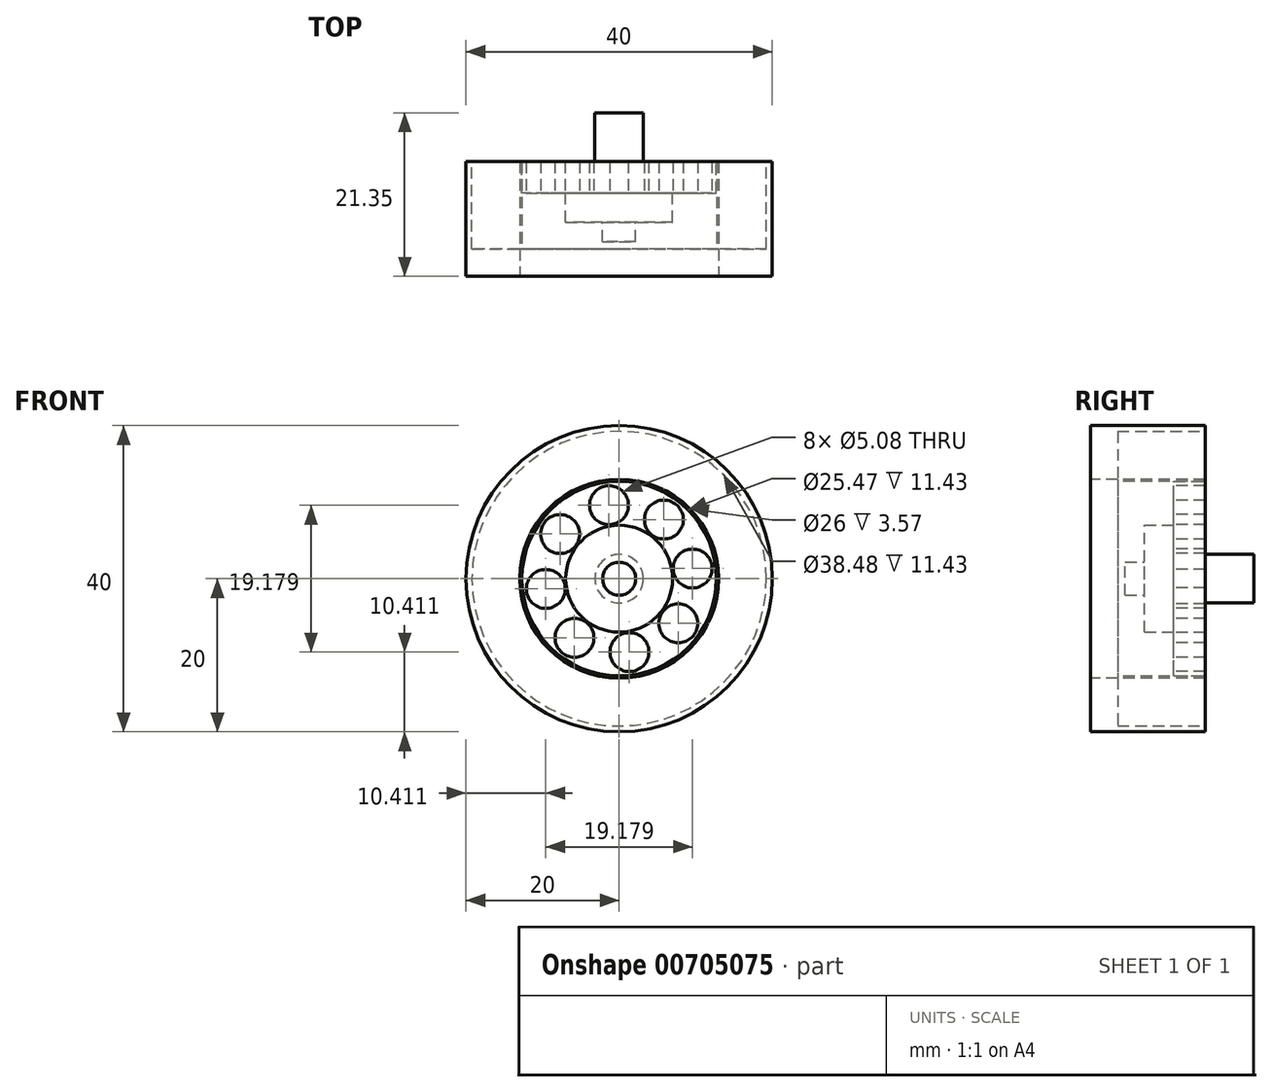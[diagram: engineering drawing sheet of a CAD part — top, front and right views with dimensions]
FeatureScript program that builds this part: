
annotation { "Feature Type Name" : "Feature", "Feature Type Description" : "" }
export const myFeature = defineFeature(function(context is Context, id is Id, definition is map)
    precondition{}
    {
        {
            var Q0;
            Q0=qCreatedBy(makeId("Front.planeOp"),FACE);
            var sketch = newSketch(context, id + "F0", { "sketchPlane" : qUnion([Q0])});
            skCircle(sketch, "E0", {"center": v(0, 0) * mm, "radius": 20 * mm});
            skCircle(sketch, "E1", {"center": v(-7.72, 5.84) * mm, "radius": 2.54 * mm});
            skCircle(sketch, "E2.1.0", {"center": v(-9.59, -1.33) * mm, "radius": 2.54 * mm});
            skCircle(sketch, "E2.2.0", {"center": v(-5.84, -7.72) * mm, "radius": 2.54 * mm});
            skCircle(sketch, "E2.3.0", {"center": v(1.33, -9.59) * mm, "radius": 2.54 * mm});
            skCircle(sketch, "E2.4.0", {"center": v(7.72, -5.84) * mm, "radius": 2.54 * mm});
            skCircle(sketch, "E2.5.0", {"center": v(9.59, 1.33) * mm, "radius": 2.54 * mm});
            skCircle(sketch, "E2.6.0", {"center": v(5.84, 7.72) * mm, "radius": 2.54 * mm});
            skCircle(sketch, "E2.7.0", {"center": v(-1.33, 9.59) * mm, "radius": 2.54 * mm});
            skSolve(sketch);
        }
        {
            var Q0;
            Q0=makeQuery(id+"F0.imprint","IMPRINT",FACE,{"disambiguationData":[TD([[makeQuery(id+"F0.imprint","IMPRINT",EDGE,{"derivedFrom":sQuery(id+"F0.wireOp",EDGE,"E0")}),1.0]])]});
            extrude(context, id + "F1", {"entities" : qUnion([Q0]), "oppositeDirection" : true, "depth" : 15 * mm, "offsetDistance" : 25.4 * mm});
        }
        {
            var Q0;
            Q0=makeQuery(id+"F0.imprint","IMPRINT",FACE,{"disambiguationData":[TD([[makeQuery(id+"F0.imprint","IMPRINT",EDGE,{"derivedFrom":sQuery(id+"F0.wireOp",EDGE,"E0")}),1.0]])]});
            var sketch = newSketch(context, id + "F2", { "sketchPlane" : qUnion([Q0])});
            skCircle(sketch, "E3", {"center": v(0, 0) * mm, "radius": 13 * mm});
            skSolve(sketch);
        }
        {
            var Q0;
            Q0=qSketchRegion(id+"F2",true);
            extrude(context, id + "F3", {"entities" : qUnion([Q0]), "operationType" : NewBodyOperationType.REMOVE, "oppositeDirection" : true, "depth" : 10.9 * mm, "offsetDistance" : 25 * mm});
        }
        {
            var Q0;
            Q0=makeQuery(id+"F3.boolean.opBoolean","COPY",FACE,{"derivedFrom":makeQuery(id+"F3.opExtrude","CAP_FACE",FACE,{"disambiguationData":[OSD([sQuery(id+"F2.wireOp",EDGE,"E3")])],"isStart":false})});
            var sketch = newSketch(context, id + "F4", { "sketchPlane" : qUnion([Q0])});
            skCircle(sketch, "E4", {"center": v(0, 0) * mm, "radius": 6.99 * mm});
            skSolve(sketch);
        }
        {
            var Q0;
            Q0=makeQuery(id+"F4.imprint","IMPRINT",FACE,{"disambiguationData":[TD([[makeQuery(id+"F4.imprint","IMPRINT",EDGE,{"derivedFrom":sQuery(id+"F4.wireOp",EDGE,"E4")}),1.0]])]});
            extrude(context, id + "F5", {"entities" : qUnion([Q0]), "operationType" : NewBodyOperationType.ADD, "depth" : 3.8 * mm, "offsetDistance" : 25.4 * mm});
        }
        {
            var Q0;
            Q0=makeQuery(id+"F5.opExtrude","CAP_FACE",FACE,{"disambiguationData":[OSD([sQuery(id+"F4.wireOp",EDGE,"E4")])],"isStart":false});
            var sketch = newSketch(context, id + "F6", { "sketchPlane" : qUnion([Q0])});
            skCircle(sketch, "E5", {"center": v(0, 0) * mm, "radius": 2.16 * mm});
            skSolve(sketch);
        }
        {
            var Q0;
            Q0=qSketchRegion(id+"F6",true);
            extrude(context, id + "F7", {"entities" : qUnion([Q0]), "operationType" : NewBodyOperationType.ADD, "depth" : 2.54 * mm, "offsetDistance" : 25.4 * mm});
        }
        {
            var Q0;
            Q0=makeQuery(id+"F1.opExtrude","CAP_FACE",FACE,{"disambiguationData":[OSD([sQuery(id+"F0.wireOp",EDGE,"E0"),sQuery(id+"F0.wireOp",EDGE,"E1"),sQuery(id+"F0.wireOp",EDGE,"E2.1.0"),sQuery(id+"F0.wireOp",EDGE,"E2.2.0"),sQuery(id+"F0.wireOp",EDGE,"E2.3.0"),sQuery(id+"F0.wireOp",EDGE,"E2.4.0"),sQuery(id+"F0.wireOp",EDGE,"E2.5.0"),sQuery(id+"F0.wireOp",EDGE,"E2.6.0"),sQuery(id+"F0.wireOp",EDGE,"E2.7.0")])],"isStart":false});
            var sketch = newSketch(context, id + "F8", { "sketchPlane" : qUnion([Q0])});
            skCircle(sketch, "E6", {"center": v(0, 0) * mm, "radius": 12.7 * mm});
            skCircle(sketch, "E7", {"center": v(0, 0) * mm, "radius": 19.24 * mm});
            skSolve(sketch);
        }
        {
            var Q0;
            Q0=makeQuery(id+"F8.imprint","IMPRINT",FACE,{"disambiguationData":[TD([[makeQuery(id+"F8.imprint","IMPRINT",EDGE,{"derivedFrom":sQuery(id+"F8.wireOp",EDGE,"E6")}),-1.0]])]});
            extrude(context, id + "F9", {"entities" : qUnion([Q0]), "operationType" : NewBodyOperationType.REMOVE, "oppositeDirection" : true, "depth" : 11.43 * mm, "offsetDistance" : 25.4 * mm});
        }
        {
            var Q0;
            {var subQ0=sQuery(id+"F0.wireOp",EDGE,"E2.3.0");var subQ1=sQuery(id+"F0.wireOp",EDGE,"E2.2.0");var subQ2=sQuery(id+"F0.wireOp",EDGE,"E2.1.0");var subQ3=sQuery(id+"F0.wireOp",EDGE,"E1");var subQ4=sQuery(id+"F0.wireOp",EDGE,"E2.4.0");var subQ5=sQuery(id+"F0.wireOp",EDGE,"E2.5.0");var subQ6=sQuery(id+"F0.wireOp",EDGE,"E2.6.0");var subQ7=sQuery(id+"F0.wireOp",EDGE,"E2.7.0");Q0=makeQuery(id+"F9.boolean.opBoolean","SPLIT",FACE,{"disambiguationData":[TD([makeQuery(id+"F1.opExtrude","SWEPT_FACE",FACE,{"disambiguationData":[OSD([subQ3])]})])],"derivedFrom":makeQuery(id+"F1.opExtrude","CAP_FACE",FACE,{"disambiguationData":[OSD([sQuery(id+"F0.wireOp",EDGE,"E0"),subQ3,subQ2,subQ1,subQ0,subQ4,subQ5,subQ6,subQ7])],"isStart":false})});}
            var sketch = newSketch(context, id + "F10", { "sketchPlane" : qUnion([Q0])});
            skCircle(sketch, "E8", {"center": v(0, 0) * mm, "radius": 3.17 * mm});
            skSolve(sketch);
        }
        {
            var Q0;
            Q0=makeQuery(id+"F10.imprint","IMPRINT",FACE,{"disambiguationData":[TD([[makeQuery(id+"F10.imprint","IMPRINT",EDGE,{"derivedFrom":sQuery(id+"F10.wireOp",EDGE,"E8")}),1.0]])]});
            extrude(context, id + "F11", {"entities" : qUnion([Q0]), "operationType" : NewBodyOperationType.ADD, "depth" : 6.35 * mm, "offsetDistance" : 25.4 * mm});
        }
        {
            var Q0;
            Q0=makeQuery(id+"F9.boolean.opBoolean","COPY",FACE,{"derivedFrom":makeQuery(id+"F9.opExtrude","CAP_FACE",FACE,{"disambiguationData":[OSD([sQuery(id+"F8.wireOp",EDGE,"E6"),sQuery(id+"F8.wireOp",EDGE,"E7")])],"isStart":false})});
            var sketch = newSketch(context, id + "F12", { "sketchPlane" : qUnion([Q0])});
            skCircle(sketch, "E9", {"center": v(0, 0) * mm, "radius": 12.97 * mm});
            skCircle(sketch, "E10", {"center": v(0, 0) * mm, "radius": 12.73 * mm});
            skSolve(sketch);
        }
        {
            var Q0;
            Q0=makeQuery(id+"F12.imprint","IMPRINT",FACE,{"disambiguationData":[TD([[makeQuery(id+"F12.imprint","IMPRINT",EDGE,{"derivedFrom":sQuery(id+"F12.wireOp",EDGE,"E9")}),1.0]])]});
            extrude(context, id + "F13", {"entities" : qUnion([Q0]), "operationType" : NewBodyOperationType.ADD, "depth" : 11.43 * mm, "offsetDistance" : 25.4 * mm});
        }
    });
